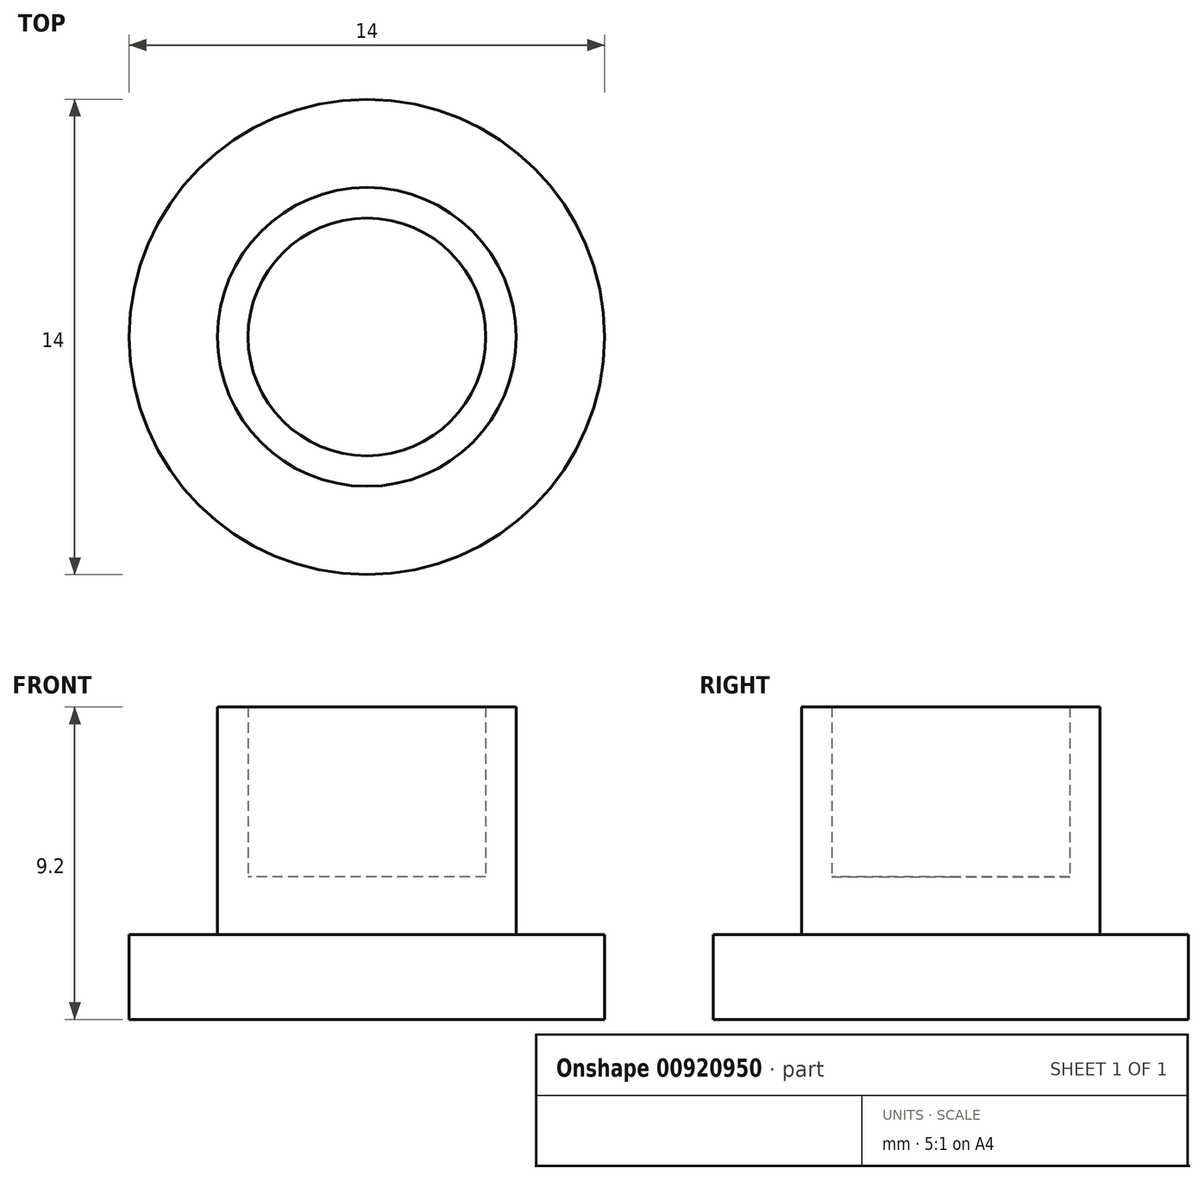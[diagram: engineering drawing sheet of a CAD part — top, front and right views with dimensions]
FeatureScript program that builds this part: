
annotation { "Feature Type Name" : "Feature", "Feature Type Description" : "" }
export const myFeature = defineFeature(function(context is Context, id is Id, definition is map)
    precondition{}
    {
        {
            var Q0;
            Q0=qCreatedBy(makeId("Top.planeOp"),FACE);
            var sketch = newSketch(context, id + "F0", { "sketchPlane" : qUnion([Q0])});
            skCircle(sketch, "E0", {"center": v(0, 0) * mm, "radius": 3.5 * mm});
            skCircle(sketch, "E1", {"center": v(0, 0) * mm, "radius": 4.4 * mm});
            skCircle(sketch, "E2", {"center": v(0, 0) * mm, "radius": 7 * mm});
            skSolve(sketch);
        }
        {
            var Q0;
            Q0=makeQuery(id+"F0.imprint","IMPRINT",FACE,{"disambiguationData":[TD([[makeQuery(id+"F0.imprint","IMPRINT",EDGE,{"derivedFrom":sQuery(id+"F0.wireOp",EDGE,"E1")}),-1.0]])]});
            extrude(context, id + "F1", {"entities" : qUnion([Q0]), "depth" : 2.5 * mm, "offsetDistance" : 25 * mm});
        }
        {
            var Q0;
            Q0=makeQuery(id+"F0.imprint","IMPRINT",FACE,{"disambiguationData":[TD([[makeQuery(id+"F0.imprint","IMPRINT",EDGE,{"derivedFrom":sQuery(id+"F0.wireOp",EDGE,"E0")}),-1.0]])]});
            var Q1;
            Q1=sQuery(id+"F0.wireOp",EDGE,"E1");
            var Q2;
            Q2=sQuery(id+"F0.wireOp",EDGE,"E0");
            extrude(context, id + "F2", {"entities" : qUnion([Q0]), "operationType" : NewBodyOperationType.ADD, "surfaceEntities" : qUnion([Q1, Q2]), "depth" : 9.2 * mm, "offsetDistance" : 25 * mm});
        }
        {
            var Q0;
            Q0=makeQuery(id+"F0.imprint","IMPRINT",FACE,{"disambiguationData":[TD([[makeQuery(id+"F0.imprint","IMPRINT",EDGE,{"derivedFrom":sQuery(id+"F0.wireOp",EDGE,"E0")}),1.0]])]});
            extrude(context, id + "F3", {"entities" : qUnion([Q0]), "operationType" : NewBodyOperationType.ADD, "depth" : 4.2 * mm, "offsetDistance" : 25 * mm});
        }
    });
